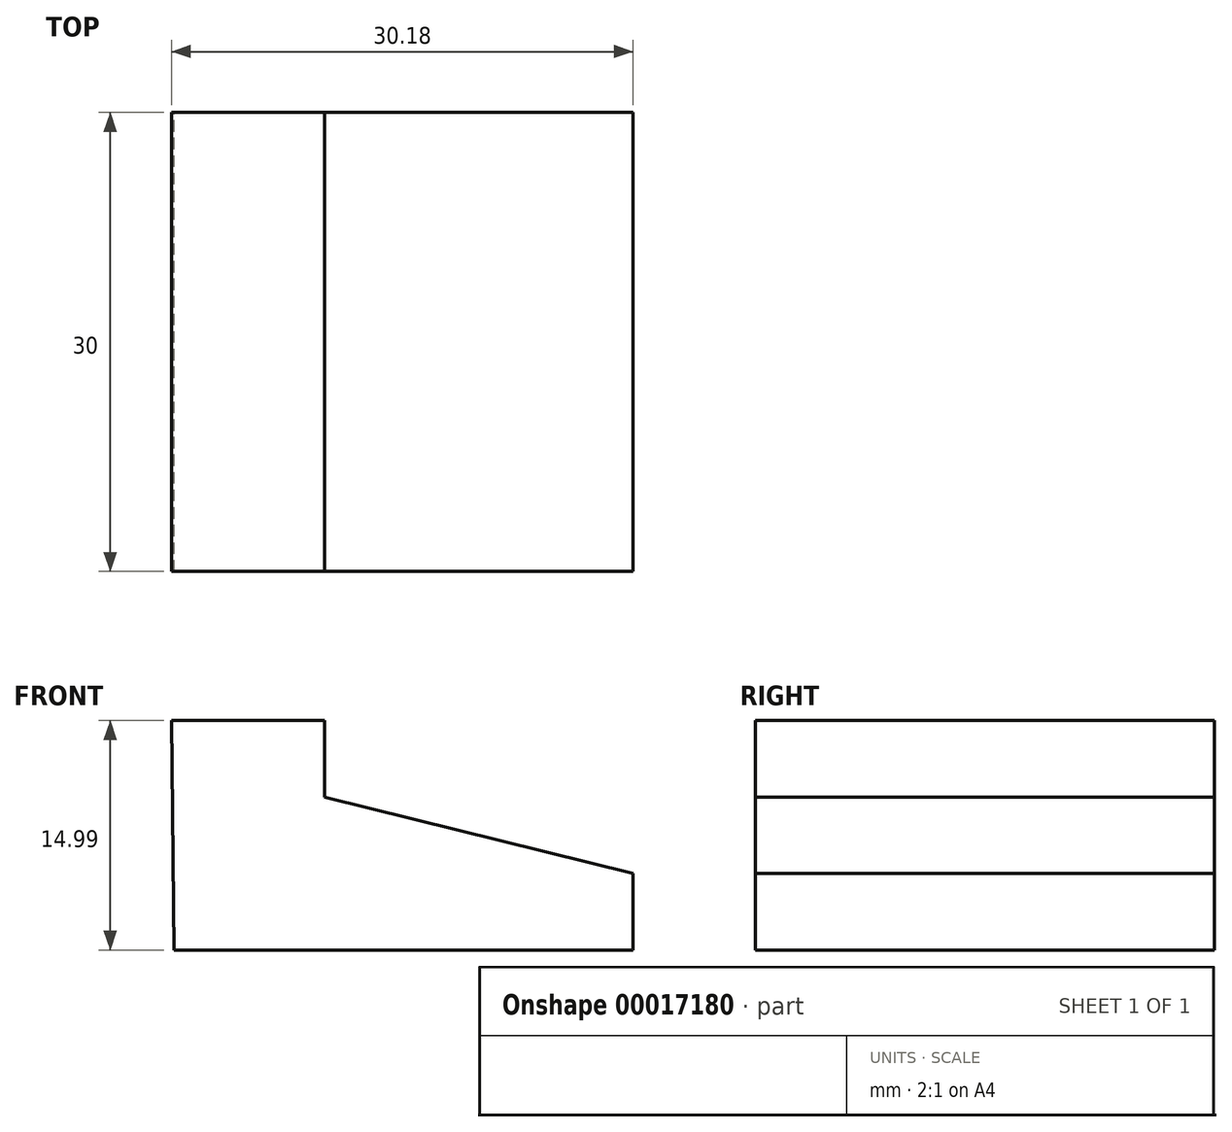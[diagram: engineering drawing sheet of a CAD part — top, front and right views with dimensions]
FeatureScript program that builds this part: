
annotation { "Feature Type Name" : "Feature", "Feature Type Description" : "" }
export const myFeature = defineFeature(function(context is Context, id is Id, definition is map)
    precondition{}
    {
        {
            var Q0;
            Q0=qCreatedBy(makeId("Front.planeOp"),FACE);
            var sketch = newSketch(context, id + "F0", { "sketchPlane" : qUnion([Q0])});
            skLineSegment(sketch, "E0", {"start": v(-13.63, 18.84) * mm, "end": v(-3.63, 18.84) * mm});
            skLineSegment(sketch, "E1", {"start": v(-3.63, 18.84) * mm, "end": v(-3.63, 13.84) * mm});
            skLineSegment(sketch, "E2", {"start": v(-3.63, 13.84) * mm, "end": v(16.55, 8.85) * mm});
            skLineSegment(sketch, "E3", {"start": v(16.55, 8.85) * mm, "end": v(16.55, 3.85) * mm});
            skLineSegment(sketch, "E4", {"start": v(16.55, 3.85) * mm, "end": v(-13.45, 3.85) * mm});
            skLineSegment(sketch, "E5", {"start": v(-13.63, 18.84) * mm, "end": v(-13.45, 3.85) * mm});
            skSolve(sketch);
        }
        {
            var Q0;
            Q0 = qSketchRegion(id + "F0", true);
            extrude(context, id + "F1", {"entities" : qUnion([Q0]), "depth" : 30 * mm});
        }
    });
